# Revit family: Murfor Compact E-70 Masonry Reinforcement
name_source: partatom
category: Specialty Equipment
revit_build: Autodesk Revit 2018 (Build: 20190510_1515(x64)
units: mm (PartAtom-declared; Revit-internal decimal feet)

## family parameters
Always vertical = Yes
Cut with Voids When Loaded = No
Part Type = Normal
Room Calculation Point = No
Round Connector Dimension = Use Diameter
Shared = No
Work Plane-Based = No

## types (2) — shared parameters
Application = Murfor Compact E-70 is made of Ausenitic Stainless steel (Molybdene - chrome - nickel alloy). This type of reinforcement has been specifically designed for exterior masonry (exposure class MX2, MX3 and MX4, compliant with Eurocode 6/EN 845-3
Datasheet = https://www.bekaert.com
Description = Compact masonry reinforcement, steel chords on interwoven fibreglass roving
Longtidinal Cord = 0.69 mm
Manufacturer = Bekaert
Material = Austenitic Stainless Steel
Material Coating Reference EN845-3 = R1
Pitch (long) - b = 7.5 mm  [stored 0.0246063 ft]
Pitch (short) - a = 5 mm  [stored 0.0164042 ft]
Steel Section Total = 9.66 mm
Step c = 33 mm  [stored 0.108268 ft]
Strain Agt = 2
Thickness - e = 1.75 mm  [stored 0.00574147 ft]
URL = https://www.bekaert.com
Weight kg/ roll = 2.65kg per roll
Width - w = 70 mm
Yield Strength - Mpa = 1300
Youngs Modulus - Gpa = 150
Z = 71.5 mm

## per-type parameters (varying)
| type | Keynote | Type Comments | Type Image |
| Murfor Compact E-70 | Suitable for all mortar joints with thickness between 3mm and 12mm | A mesh consisiting of 14 steel cords. | Murfor Compact E-70.PNG |
| Murfor Compact E-70 Masonry Reinforcement | A mesh consisiting of 14 steel cords. | Suitable for all mortar joints with thickness between 3mm and 12mm | <None> |

note: [stored X ft] marks values corroborated as IEEE doubles in the binary element streams (Revit-internal decimal feet)

## geometry (parser evidence)
native form markers: Blend x2, Sweep x13
no freeform markers — native parametric forms only
